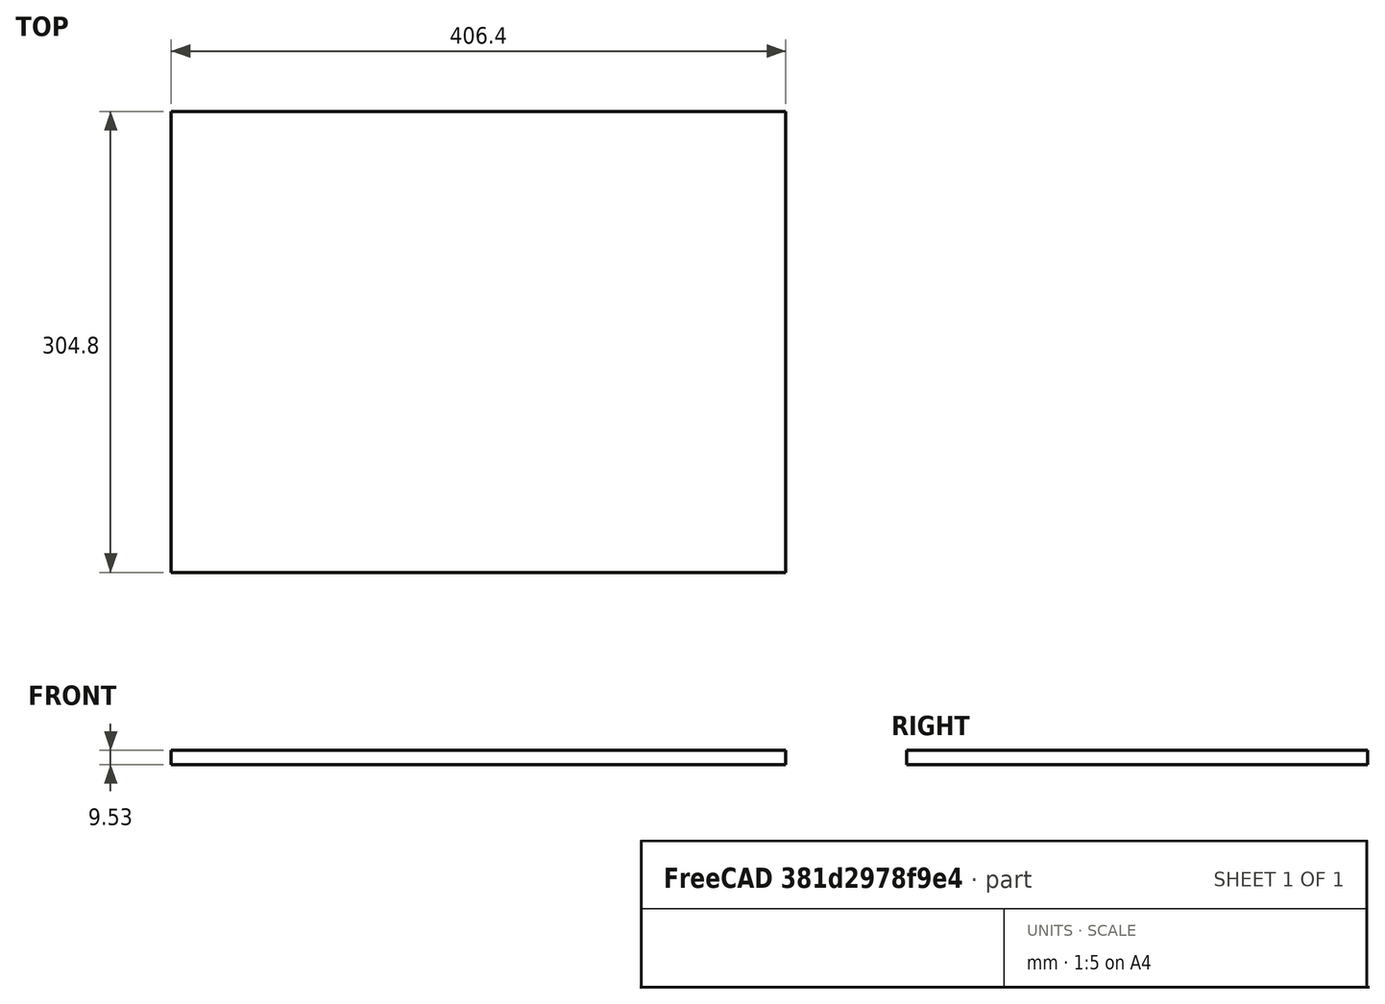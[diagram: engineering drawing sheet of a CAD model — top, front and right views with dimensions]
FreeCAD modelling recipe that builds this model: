
FCSTD DOCUMENT  (FreeCAD 0.16RUnknown)
Label: Generic
License: All rights reserved
LicenseURL: http://en.wikipedia.org/wiki/All_rights_reserved
objects: Sketcher::SketchObject×1, Part::Extrusion×1
note: 2 computed .brp shape members not serialized (recipe doc carries the construction recipe); baked Part::Feature solids carry a one-line shape summary decoded from their .brp

FEATURE [Sketcher::SketchObject] Sketch
  sketch-geometry (4):
    g0: LineSegment StartX=0 StartY=0 StartZ=0 EndX=406.4 EndY=0 EndZ=0
    g1: LineSegment StartX=406.4 StartY=0 StartZ=0 EndX=406.4 EndY=304.8 EndZ=0
    g2: LineSegment StartX=406.4 StartY=304.8 StartZ=0 EndX=0 EndY=304.8 EndZ=0
    g3: LineSegment StartX=0 StartY=304.8 StartZ=0 EndX=0 EndY=0 EndZ=0
  constraints (11):
    c: Coincident(g0,g1)
    c: Coincident(g1,g2)
    c: Coincident(g2,g3)
    c: Coincident(g3,g0)
    c: Horizontal(g0)
    c: Horizontal(g2)
    c: Vertical(g1)
    c: Vertical(g3)
    c: Coincident(g0,g-1)
    c: DistanceX(g0,g0) = 406.4
    c: DistanceY(g3,g3) = 304.8
FEATURE [Part::Extrusion] Extrude
  Base = -> Sketch
  Dir = (0,0,9.525)
  Solid = true
